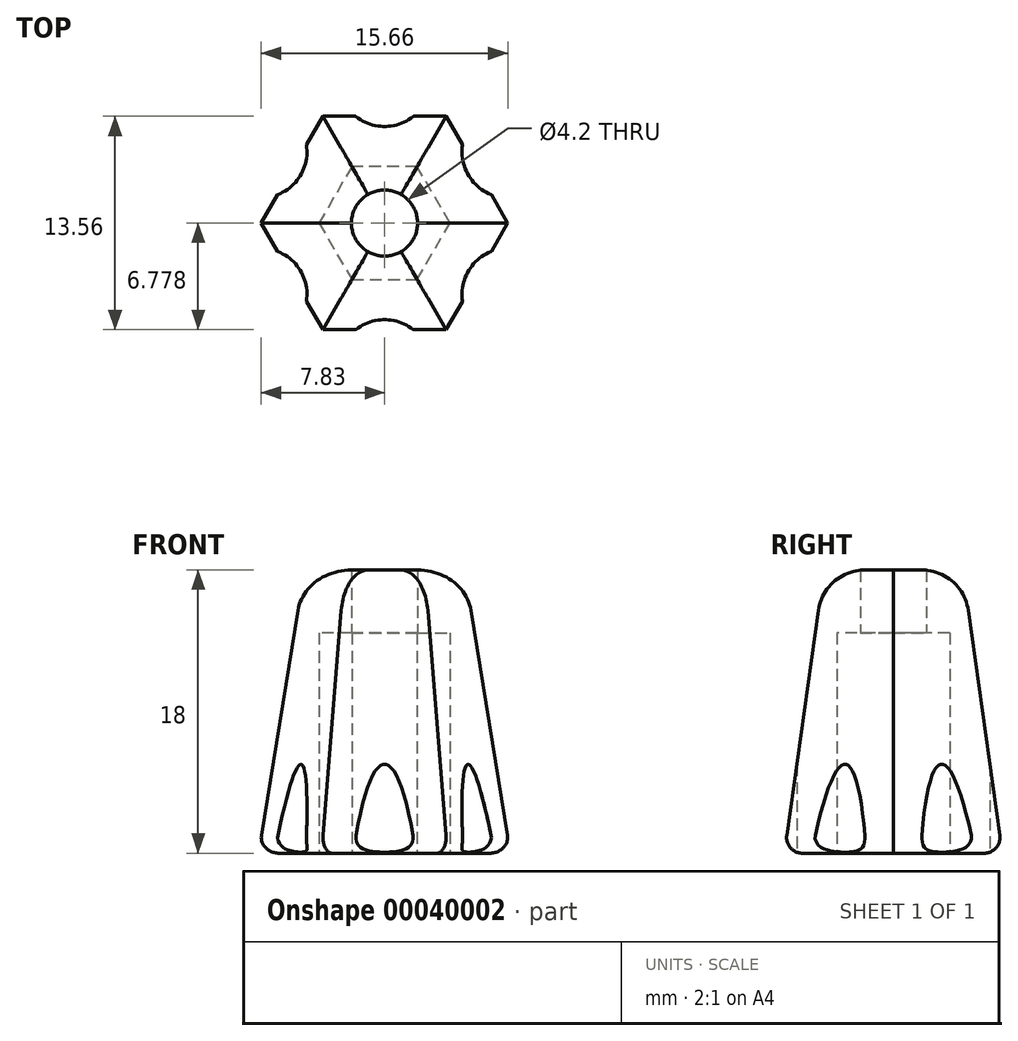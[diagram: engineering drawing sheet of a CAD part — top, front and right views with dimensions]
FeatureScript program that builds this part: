
annotation { "Feature Type Name" : "Feature", "Feature Type Description" : "" }
export const myFeature = defineFeature(function(context is Context, id is Id, definition is map)
    precondition{}
    {
        {
            var Q0;
            Q0=qCreatedBy(makeId("Top.planeOp"),FACE);
            var sketch = newSketch(context, id + "F0", { "sketchPlane" : qUnion([Q0])});
            skLineSegment(sketch, "E0", {"start": v(0, 0) * mm, "end": v(8, 0) * mm});
            skLineSegment(sketch, "E1", {"start": v(8, 0) * mm, "end": v(12, 6.93) * mm});
            skLineSegment(sketch, "E2", {"start": v(12, 6.93) * mm, "end": v(8, 13.86) * mm});
            skLineSegment(sketch, "E3", {"start": v(8, 13.86) * mm, "end": v(0, 13.86) * mm});
            skLineSegment(sketch, "E4", {"start": v(0, 13.86) * mm, "end": v(-4, 6.93) * mm});
            skLineSegment(sketch, "E5", {"start": v(-4, 6.93) * mm, "end": v(0, 0) * mm});
            skCircle(sketch, "E6", {"center": v(4, 6.93) * mm, "radius": 8 * mm, "construction": true});
            skSolve(sketch);
        }
        {
            var Q0;
            Q0=qCreatedBy(makeId("Top.planeOp"),FACE);
            var sketch = newSketch(context, id + "F1", { "sketchPlane" : qUnion([Q0])});
            skCircle(sketch, "E7", {"center": v(4, 6.93) * mm, "radius": 4.15 * mm, "construction": true});
            skLineSegment(sketch, "E8", {"start": v(-0.15, 6.93) * mm, "end": v(1.93, 3.33) * mm});
            skLineSegment(sketch, "E9", {"start": v(8.15, 6.93) * mm, "end": v(6.07, 10.52) * mm});
            skLineSegment(sketch, "E10", {"start": v(1.93, 10.52) * mm, "end": v(-0.15, 6.93) * mm});
            skLineSegment(sketch, "E11", {"start": v(6.08, 3.33) * mm, "end": v(8.15, 6.93) * mm});
            skLineSegment(sketch, "E12", {"start": v(6.08, 10.52) * mm, "end": v(1.93, 10.52) * mm});
            skLineSegment(sketch, "E13", {"start": v(1.92, 3.33) * mm, "end": v(6.08, 3.33) * mm});
            skLineSegment(sketch, "E14.0", {"start": v(8, 0) * mm, "end": v(9, 1.73) * mm});
            skLineSegment(sketch, "E15", {"start": v(10, 3.46) * mm, "end": v(13.66, 1.35) * mm, "construction": true});
            skArc(sketch, "E16", {"start": v(11, 5.2) * mm, "mid": v(9.31, 3.86) * mm, "end": v(9, 1.73) * mm});
            skLineSegment(sketch, "E17", {"start": v(9, 1.73) * mm, "end": v(10, 3.46) * mm});
            skLineSegment(sketch, "E18", {"start": v(10, 3.46) * mm, "end": v(11, 5.2) * mm});
            skLineSegment(sketch, "E19", {"start": v(11, 5.2) * mm, "end": v(12, 6.93) * mm});
            skLineSegment(sketch, "E20", {"start": v(9, 1.73) * mm, "end": v(11, 5.2) * mm});
            skArc(sketch, "E21.1.0", {"start": v(9, 12.12) * mm, "mid": v(9.31, 10) * mm, "end": v(11, 8.66) * mm});
            skLineSegment(sketch, "E21.1.1", {"start": v(11, 8.66) * mm, "end": v(10, 10.4) * mm});
            skLineSegment(sketch, "E21.1.2", {"start": v(10, 10.4) * mm, "end": v(9, 12.12) * mm});
            skArc(sketch, "E21.2.0", {"start": v(2, 13.86) * mm, "mid": v(4, 13.06) * mm, "end": v(6, 13.86) * mm});
            skLineSegment(sketch, "E21.2.1", {"start": v(6, 13.86) * mm, "end": v(4, 13.86) * mm});
            skLineSegment(sketch, "E21.2.2", {"start": v(4, 13.86) * mm, "end": v(2, 13.86) * mm});
            skArc(sketch, "E21.3.0", {"start": v(-3, 8.66) * mm, "mid": v(-1.31, 10) * mm, "end": v(-1, 12.12) * mm});
            skLineSegment(sketch, "E21.3.1", {"start": v(-1, 12.12) * mm, "end": v(-2, 10.4) * mm});
            skLineSegment(sketch, "E21.3.2", {"start": v(-2, 10.4) * mm, "end": v(-3, 8.66) * mm});
            skArc(sketch, "E21.4.0", {"start": v(-1, 1.73) * mm, "mid": v(-1.31, 3.86) * mm, "end": v(-3, 5.2) * mm});
            skLineSegment(sketch, "E21.4.1", {"start": v(-3, 5.2) * mm, "end": v(-2, 3.46) * mm});
            skLineSegment(sketch, "E21.4.2", {"start": v(-2, 3.46) * mm, "end": v(-1, 1.73) * mm});
            skArc(sketch, "E21.5.0", {"start": v(6, 0) * mm, "mid": v(4, 0.8) * mm, "end": v(2, 0) * mm});
            skLineSegment(sketch, "E21.5.1", {"start": v(2, 0) * mm, "end": v(4, 0) * mm});
            skLineSegment(sketch, "E21.5.2", {"start": v(4, 0) * mm, "end": v(6, 0) * mm});
            skSolve(sketch);
        }
        {
            var Q0;
            Q0=qSketchRegion(id+"F0",true);
            extrude(context, id + "F2", {"entities" : qUnion([Q0]), "depth" : 18 * mm, "hasDraft" : true, "draftAngle" : 8 * degree, "draftPullDirection" : true});
        }
        {
            var Q0;
            Q0=makeQuery(id+"F2.opExtrude","CAP_FACE",FACE,{"disambiguationData":[OSD([sQuery(id+"F0.wireOp",EDGE,"E0"),sQuery(id+"F0.wireOp",EDGE,"E1"),sQuery(id+"F0.wireOp",EDGE,"E2"),sQuery(id+"F0.wireOp",EDGE,"E3"),sQuery(id+"F0.wireOp",EDGE,"E4"),sQuery(id+"F0.wireOp",EDGE,"E5")])],"isStart":false});
            fillet(context, id + "F3", {"entities" : qUnion([Q0]), "radius" : 3 * mm, "tangentPropagation" : true, "allowEdgeOverflow" : false});
        }
        {
            var Q0;
            Q0=qSketchRegion(id+"F1",true);
            extrude(context, id + "F4", {"entities" : qUnion([Q0]), "operationType" : NewBodyOperationType.REMOVE, "depth" : 14 * mm});
        }
        {
            var Q0;
            Q0=makeQuery(id+"F4.boolean.opBoolean","COPY",FACE,{"derivedFrom":makeQuery(id+"F4.opExtrude","CAP_FACE",FACE,{"disambiguationData":[OSD([sQuery(id+"F1.wireOp",EDGE,"E8"),sQuery(id+"F1.wireOp",EDGE,"E9"),sQuery(id+"F1.wireOp",EDGE,"E10"),sQuery(id+"F1.wireOp",EDGE,"E11"),sQuery(id+"F1.wireOp",EDGE,"E12"),sQuery(id+"F1.wireOp",EDGE,"E13")])],"isStart":false})});
            var sketch = newSketch(context, id + "F5", { "sketchPlane" : qUnion([Q0])});
            skCircle(sketch, "E22", {"center": v(4, -6.93) * mm, "radius": 2.1 * mm});
            skPoint(sketch, "E22.centerSnap0", {"position": v(4, -3.33) * mm});
            skSolve(sketch);
        }
        {
            var Q0;
            Q0=qSketchRegion(id+"F5",true);
            var Q1;
            Q1=sQuery(id+"F5.wireOp",EDGE,"E22");
            extrude(context, id + "F6", {"entities" : qUnion([Q0]), "operationType" : NewBodyOperationType.REMOVE, "surfaceEntities" : qUnion([Q1]), "endBound" : BoundingType.THROUGH_ALL, "oppositeDirection" : true, "depth" : 10.62 * mm});
        }
        {
            var Q0;
            {var subQ0=sQuery(id+"F0.wireOp",EDGE,"E3");var subQ1=sQuery(id+"F0.wireOp",EDGE,"E4");Q0=makeQuery(id+"F4.boolean.opBoolean","SPLIT",EDGE,{"disambiguationData":[TD([makeQuery(id+"F2.opExtrude","SWEPT_FACE",FACE,{"disambiguationData":[OSD([subQ1])]})])],"derivedFrom":makeQuery(id+"F2.opExtrude","CAP_EDGE",EDGE,{"disambiguationData":[OSD([subQ0])],"isStart":true})});}
            var Q1;
            {var subQ0=sQuery(id+"F0.wireOp",EDGE,"E4");var subQ1=sQuery(id+"F0.wireOp",EDGE,"E3");Q1=makeQuery(id+"F4.boolean.opBoolean","SPLIT",EDGE,{"disambiguationData":[TD([makeQuery(id+"F2.opExtrude","SWEPT_FACE",FACE,{"disambiguationData":[OSD([subQ1])]})])],"derivedFrom":makeQuery(id+"F2.opExtrude","CAP_EDGE",EDGE,{"disambiguationData":[OSD([subQ0])],"isStart":true})});}
            var Q2;
            Q2=makeQuery(id+"F4.boolean.opBoolean","COPY",EDGE,{"derivedFrom":makeQuery(id+"F4.opExtrude","CAP_EDGE",EDGE,{"disambiguationData":[OSD([sQuery(id+"F1.wireOp",EDGE,"E21.3.0")])],"isStart":true})});
            var Q3;
            {var subQ0=sQuery(id+"F0.wireOp",EDGE,"E4");var subQ1=sQuery(id+"F0.wireOp",EDGE,"E5");Q3=makeQuery(id+"F4.boolean.opBoolean","SPLIT",EDGE,{"disambiguationData":[TD([makeQuery(id+"F2.opExtrude","SWEPT_FACE",FACE,{"disambiguationData":[OSD([subQ1])]})])],"derivedFrom":makeQuery(id+"F2.opExtrude","CAP_EDGE",EDGE,{"disambiguationData":[OSD([subQ0])],"isStart":true})});}
            var Q4;
            {var subQ0=sQuery(id+"F0.wireOp",EDGE,"E5");var subQ1=sQuery(id+"F0.wireOp",EDGE,"E4");Q4=makeQuery(id+"F4.boolean.opBoolean","SPLIT",EDGE,{"disambiguationData":[TD([makeQuery(id+"F2.opExtrude","SWEPT_FACE",FACE,{"disambiguationData":[OSD([subQ1])]})])],"derivedFrom":makeQuery(id+"F2.opExtrude","CAP_EDGE",EDGE,{"disambiguationData":[OSD([subQ0])],"isStart":true})});}
            var Q5;
            Q5=makeQuery(id+"F4.boolean.opBoolean","COPY",EDGE,{"derivedFrom":makeQuery(id+"F4.opExtrude","CAP_EDGE",EDGE,{"disambiguationData":[OSD([sQuery(id+"F1.wireOp",EDGE,"E21.4.0")])],"isStart":true})});
            var Q6;
            {var subQ0=sQuery(id+"F0.wireOp",EDGE,"E5");var subQ1=sQuery(id+"F0.wireOp",EDGE,"E0");Q6=makeQuery(id+"F4.boolean.opBoolean","SPLIT",EDGE,{"disambiguationData":[TD([makeQuery(id+"F2.opExtrude","SWEPT_FACE",FACE,{"disambiguationData":[OSD([subQ1])]})])],"derivedFrom":makeQuery(id+"F2.opExtrude","CAP_EDGE",EDGE,{"disambiguationData":[OSD([subQ0])],"isStart":true})});}
            var Q7;
            {var subQ0=sQuery(id+"F0.wireOp",EDGE,"E0");var subQ1=sQuery(id+"F0.wireOp",EDGE,"E5");Q7=makeQuery(id+"F4.boolean.opBoolean","SPLIT",EDGE,{"disambiguationData":[TD([makeQuery(id+"F2.opExtrude","SWEPT_FACE",FACE,{"disambiguationData":[OSD([subQ1])]})])],"derivedFrom":makeQuery(id+"F2.opExtrude","CAP_EDGE",EDGE,{"disambiguationData":[OSD([subQ0])],"isStart":true})});}
            var Q8;
            Q8=makeQuery(id+"F4.boolean.opBoolean","COPY",EDGE,{"derivedFrom":makeQuery(id+"F4.opExtrude","CAP_EDGE",EDGE,{"disambiguationData":[OSD([sQuery(id+"F1.wireOp",EDGE,"E21.5.0")])],"isStart":true})});
            var Q9;
            {var subQ0=sQuery(id+"F0.wireOp",EDGE,"E0");var subQ1=sQuery(id+"F0.wireOp",EDGE,"E1");Q9=makeQuery(id+"F4.boolean.opBoolean","SPLIT",EDGE,{"disambiguationData":[TD([makeQuery(id+"F2.opExtrude","SWEPT_FACE",FACE,{"disambiguationData":[OSD([subQ1])]})])],"derivedFrom":makeQuery(id+"F2.opExtrude","CAP_EDGE",EDGE,{"disambiguationData":[OSD([subQ0])],"isStart":true})});}
            var Q10;
            {var subQ0=sQuery(id+"F0.wireOp",EDGE,"E1");var subQ1=sQuery(id+"F0.wireOp",EDGE,"E0");Q10=makeQuery(id+"F4.boolean.opBoolean","SPLIT",EDGE,{"disambiguationData":[TD([makeQuery(id+"F2.opExtrude","SWEPT_FACE",FACE,{"disambiguationData":[OSD([subQ1])]})])],"derivedFrom":makeQuery(id+"F2.opExtrude","CAP_EDGE",EDGE,{"disambiguationData":[OSD([subQ0])],"isStart":true})});}
            var Q11;
            Q11=makeQuery(id+"F4.boolean.opBoolean","COPY",EDGE,{"derivedFrom":makeQuery(id+"F4.opExtrude","CAP_EDGE",EDGE,{"disambiguationData":[OSD([sQuery(id+"F1.wireOp",EDGE,"E16")])],"isStart":true})});
            var Q12;
            {var subQ0=sQuery(id+"F0.wireOp",EDGE,"E1");var subQ1=sQuery(id+"F0.wireOp",EDGE,"E2");Q12=makeQuery(id+"F4.boolean.opBoolean","SPLIT",EDGE,{"disambiguationData":[TD([makeQuery(id+"F2.opExtrude","SWEPT_FACE",FACE,{"disambiguationData":[OSD([subQ1])]})])],"derivedFrom":makeQuery(id+"F2.opExtrude","CAP_EDGE",EDGE,{"disambiguationData":[OSD([subQ0])],"isStart":true})});}
            var Q13;
            {var subQ0=sQuery(id+"F0.wireOp",EDGE,"E2");var subQ1=sQuery(id+"F0.wireOp",EDGE,"E1");Q13=makeQuery(id+"F4.boolean.opBoolean","SPLIT",EDGE,{"disambiguationData":[TD([makeQuery(id+"F2.opExtrude","SWEPT_FACE",FACE,{"disambiguationData":[OSD([subQ1])]})])],"derivedFrom":makeQuery(id+"F2.opExtrude","CAP_EDGE",EDGE,{"disambiguationData":[OSD([subQ0])],"isStart":true})});}
            var Q14;
            Q14=makeQuery(id+"F4.boolean.opBoolean","COPY",EDGE,{"derivedFrom":makeQuery(id+"F4.opExtrude","CAP_EDGE",EDGE,{"disambiguationData":[OSD([sQuery(id+"F1.wireOp",EDGE,"E21.1.0")])],"isStart":true})});
            var Q15;
            {var subQ0=sQuery(id+"F0.wireOp",EDGE,"E2");var subQ1=sQuery(id+"F0.wireOp",EDGE,"E3");Q15=makeQuery(id+"F4.boolean.opBoolean","SPLIT",EDGE,{"disambiguationData":[TD([makeQuery(id+"F2.opExtrude","SWEPT_FACE",FACE,{"disambiguationData":[OSD([subQ1])]})])],"derivedFrom":makeQuery(id+"F2.opExtrude","CAP_EDGE",EDGE,{"disambiguationData":[OSD([subQ0])],"isStart":true})});}
            var Q16;
            {var subQ0=sQuery(id+"F0.wireOp",EDGE,"E3");var subQ1=sQuery(id+"F0.wireOp",EDGE,"E2");Q16=makeQuery(id+"F4.boolean.opBoolean","SPLIT",EDGE,{"disambiguationData":[TD([makeQuery(id+"F2.opExtrude","SWEPT_FACE",FACE,{"disambiguationData":[OSD([subQ1])]})])],"derivedFrom":makeQuery(id+"F2.opExtrude","CAP_EDGE",EDGE,{"disambiguationData":[OSD([subQ0])],"isStart":true})});}
            var Q17;
            Q17=makeQuery(id+"F4.boolean.opBoolean","COPY",EDGE,{"derivedFrom":makeQuery(id+"F4.opExtrude","CAP_EDGE",EDGE,{"disambiguationData":[OSD([sQuery(id+"F1.wireOp",EDGE,"E21.2.0")])],"isStart":true})});
            fillet(context, id + "F7", {"entities" : qUnion([Q0, Q1, Q2, Q3, Q4, Q5, Q6, Q7, Q8, Q9, Q10, Q11, Q12, Q13, Q14, Q15, Q16, Q17]), "radius" : 1 * mm, "tangentPropagation" : true, "allowEdgeOverflow" : false});
        }
    });
